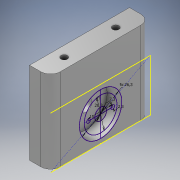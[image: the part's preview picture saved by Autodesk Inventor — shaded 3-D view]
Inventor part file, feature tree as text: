
AUTODESK INVENTOR PART (.ipt)
format: ipt  version: 2020 (Build 240168000, 168)  size: 214,016 bytes
history: native  units: mm
features: extrude x6, sketch x5, other x1, fillet x1, chamfer x1, projected_geometry x1
ambient origin geometry x8: Origin, YZ Plane, XZ Plane, XY Plane, X Axis, Y Axis, Z Axis, Center Point
bodies: Body1 (feature_tree)
feature tree (15):
  other  "Твердое тело1"
  extrude  "Выдавливание1"  Depth=13.0mm
  sketch  "Эскиз2"
  extrude  "Выдавливание3"  Depth=62.0mm
  extrude  "Выдавливание4"  Depth=16.0mm
  extrude  "Выдавливание5"  Depth=4.0mm
  fillet  "Сопряжение1"  [1 undecoded]
  chamfer  "Фаска1"  Distance=20.3mm
  extrude  "Выдавливание6"  Depth=2.3mm
  extrude  "Выдавливание7"  Depth=15.0mm
  sketch  "Эскиз1"
  sketch  "Эскиз3"
  sketch  "Эскиз6"
  projected_geometry  "Спроецированная петля2"
  sketch  "Эскиз7"
note: 1 required parameter value undecoded (feature->parameter linkage not recoverable at this tier; creation-order binding heuristic only, values carry confidence <= 0.55)
